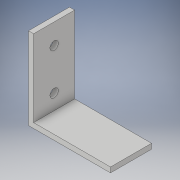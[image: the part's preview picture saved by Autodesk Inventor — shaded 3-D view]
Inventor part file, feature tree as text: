
AUTODESK INVENTOR PART (.ipt)
format: ipt  version: 2018 (Build 220112000, 112)  size: 110,592 bytes
history: native  units: in
note: dims shown in document units (in); Inventor stores cm internally (conversion verified against a paired STEP export)
features: extrude x2, sketch x2
ambient origin geometry x8: Origin, YZ Plane, XZ Plane, XY Plane, X Axis, Y Axis, Z Axis, Center Point
bodies: Solid1 (feature_tree)
feature tree (4):
  extrude  "Extrusion1"  Depth=2.0in
  extrude  "Extrusion2"  Depth=0.125in
  sketch  "Sketch1"  dims[d0=0.125in d1=2.0in]
  sketch  "Sketch2"  dims[d2=2.0in d3=0.125in d4=1.0in d5=0.0in d6=0.5in d7=1.0in d8=0.2031in d9=1.0in d10=0.0in]
